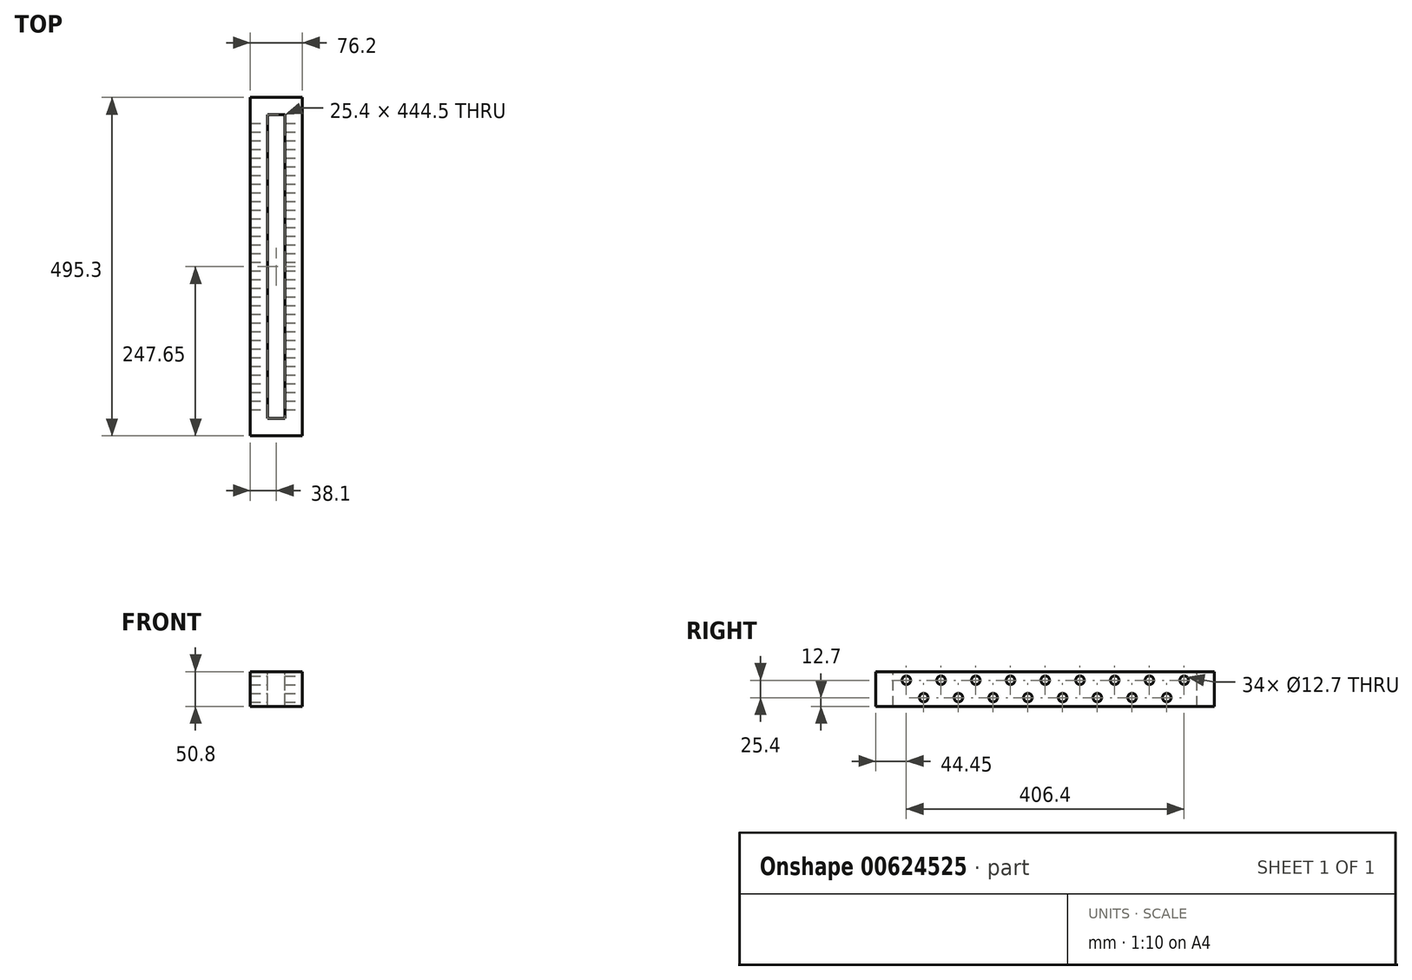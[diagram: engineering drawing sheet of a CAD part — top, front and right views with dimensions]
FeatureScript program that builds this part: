
annotation { "Feature Type Name" : "Feature", "Feature Type Description" : "" }
export const myFeature = defineFeature(function(context is Context, id is Id, definition is map)
    precondition{}
    {
        {
            var Q0;
            Q0=qCreatedBy(makeId("Front.planeOp"),FACE);
            var sketch = newSketch(context, id + "F0", { "sketchPlane" : qUnion([Q0])});
            skLineSegment(sketch, "E0.bottom", {"start": v(0, 0) * mm, "end": v(76.2, 0) * mm});
            skLineSegment(sketch, "E0.top", {"start": v(0, -50.8) * mm, "end": v(76.2, -50.8) * mm});
            skLineSegment(sketch, "E0.left", {"start": v(0, 0) * mm, "end": v(0, -50.8) * mm});
            skLineSegment(sketch, "E0.right", {"start": v(76.2, 0) * mm, "end": v(76.2, -50.8) * mm});
            skSolve(sketch);
        }
        {
            var Q0;
            Q0=makeQuery(id+"F0.imprint","IMPRINT",FACE,{"disambiguationData":[TD([[makeQuery(id+"F0.imprint","IMPRINT",EDGE,{"derivedFrom":sQuery(id+"F0.wireOp",EDGE,"E0.bottom")}),-1.0]])]});
            extrude(context, id + "F1", {"entities" : qUnion([Q0]), "depth" : 495.3 * mm, "offsetDistance" : 25.4 * mm});
        }
        {
            var Q0;
            Q0=makeQuery(id+"F1.opExtrude","SWEPT_FACE",FACE,{"disambiguationData":[OSD([sQuery(id+"F0.wireOp",EDGE,"E0.bottom")])]});
            var sketch = newSketch(context, id + "F2", { "sketchPlane" : qUnion([Q0])});
            skLineSegment(sketch, "E1.bottom", {"start": v(50.8, -469.9) * mm, "end": v(25.4, -469.9) * mm});
            skLineSegment(sketch, "E1.top", {"start": v(50.8, -25.4) * mm, "end": v(25.4, -25.4) * mm});
            skLineSegment(sketch, "E1.left", {"start": v(50.8, -469.9) * mm, "end": v(50.8, -25.4) * mm});
            skLineSegment(sketch, "E1.right", {"start": v(25.4, -469.9) * mm, "end": v(25.4, -25.4) * mm});
            skSolve(sketch);
        }
        {
            var Q0;
            Q0=makeQuery(id+"F2.imprint","IMPRINT",FACE,{"disambiguationData":[TD([[makeQuery(id+"F2.imprint","IMPRINT",EDGE,{"derivedFrom":sQuery(id+"F2.wireOp",EDGE,"E1.bottom")}),-1.0]])]});
            extrude(context, id + "F3", {"entities" : qUnion([Q0]), "operationType" : NewBodyOperationType.REMOVE, "oppositeDirection" : true, "depth" : 50.8 * mm, "offsetDistance" : 25.4 * mm});
        }
        {
            var Q0;
            Q0=makeQuery(id+"F1.opExtrude","SWEPT_FACE",FACE,{"disambiguationData":[OSD([sQuery(id+"F0.wireOp",EDGE,"E0.right")])]});
            var sketch = newSketch(context, id + "F4", { "sketchPlane" : qUnion([Q0])});
            skCircle(sketch, "E2", {"center": v(-450.85, -12.7) * mm, "radius": 6.35 * mm});
            skCircle(sketch, "E3.1.0.0", {"center": v(-400.05, -12.7) * mm, "radius": 6.35 * mm});
            skCircle(sketch, "E3.2.0.0", {"center": v(-349.25, -12.7) * mm, "radius": 6.35 * mm});
            skCircle(sketch, "E3.3.0.0", {"center": v(-298.45, -12.7) * mm, "radius": 6.35 * mm});
            skCircle(sketch, "E3.4.0.0", {"center": v(-247.65, -12.7) * mm, "radius": 6.35 * mm});
            skCircle(sketch, "E3.5.0.0", {"center": v(-196.85, -12.7) * mm, "radius": 6.35 * mm});
            skCircle(sketch, "E3.6.0.0", {"center": v(-146.05, -12.7) * mm, "radius": 6.35 * mm});
            skCircle(sketch, "E3.7.0.0", {"center": v(-95.25, -12.7) * mm, "radius": 6.35 * mm});
            skCircle(sketch, "E3.8.0.0", {"center": v(-44.45, -12.7) * mm, "radius": 6.35 * mm});
            skLineSegment(sketch, "E3.direction1", {"start": v(-450.85, -12.7) * mm, "end": v(-400.05, -12.7) * mm, "construction": true});
            skCircle(sketch, "E4", {"center": v(-425.45, -38.1) * mm, "radius": 6.35 * mm});
            skCircle(sketch, "E5.1.0.0", {"center": v(-374.65, -38.1) * mm, "radius": 6.35 * mm});
            skCircle(sketch, "E5.2.0.0", {"center": v(-323.85, -38.1) * mm, "radius": 6.35 * mm});
            skCircle(sketch, "E5.3.0.0", {"center": v(-273.05, -38.1) * mm, "radius": 6.35 * mm});
            skCircle(sketch, "E5.4.0.0", {"center": v(-222.25, -38.1) * mm, "radius": 6.35 * mm});
            skCircle(sketch, "E5.5.0.0", {"center": v(-171.45, -38.1) * mm, "radius": 6.35 * mm});
            skCircle(sketch, "E5.6.0.0", {"center": v(-120.65, -38.1) * mm, "radius": 6.35 * mm});
            skCircle(sketch, "E5.7.0.0", {"center": v(-69.85, -38.1) * mm, "radius": 6.35 * mm});
            skLineSegment(sketch, "E5.direction1", {"start": v(-425.45, -38.1) * mm, "end": v(-374.65, -38.1) * mm, "construction": true});
            skSolve(sketch);
        }
        {
            var Q0;
            Q0=makeQuery(id+"F4.imprint","IMPRINT",FACE,{"disambiguationData":[TD([[makeQuery(id+"F4.imprint","IMPRINT",EDGE,{"derivedFrom":sQuery(id+"F4.wireOp",EDGE,"E2")}),1.0]])]});
            var Q1;
            Q1=makeQuery(id+"F4.imprint","IMPRINT",FACE,{"disambiguationData":[TD([[makeQuery(id+"F4.imprint","IMPRINT",EDGE,{"derivedFrom":sQuery(id+"F4.wireOp",EDGE,"E3.1.0.0")}),1.0]])]});
            var Q2;
            Q2=makeQuery(id+"F4.imprint","IMPRINT",FACE,{"disambiguationData":[TD([[makeQuery(id+"F4.imprint","IMPRINT",EDGE,{"derivedFrom":sQuery(id+"F4.wireOp",EDGE,"E3.2.0.0")}),1.0]])]});
            var Q3;
            Q3=makeQuery(id+"F4.imprint","IMPRINT",FACE,{"disambiguationData":[TD([[makeQuery(id+"F4.imprint","IMPRINT",EDGE,{"derivedFrom":sQuery(id+"F4.wireOp",EDGE,"E3.3.0.0")}),1.0]])]});
            var Q4;
            Q4=makeQuery(id+"F4.imprint","IMPRINT",FACE,{"disambiguationData":[TD([[makeQuery(id+"F4.imprint","IMPRINT",EDGE,{"derivedFrom":sQuery(id+"F4.wireOp",EDGE,"E3.4.0.0")}),1.0]])]});
            var Q5;
            Q5=makeQuery(id+"F4.imprint","IMPRINT",FACE,{"disambiguationData":[TD([[makeQuery(id+"F4.imprint","IMPRINT",EDGE,{"derivedFrom":sQuery(id+"F4.wireOp",EDGE,"E3.5.0.0")}),1.0]])]});
            var Q6;
            Q6=makeQuery(id+"F4.imprint","IMPRINT",FACE,{"disambiguationData":[TD([[makeQuery(id+"F4.imprint","IMPRINT",EDGE,{"derivedFrom":sQuery(id+"F4.wireOp",EDGE,"E3.6.0.0")}),1.0]])]});
            var Q7;
            Q7=makeQuery(id+"F4.imprint","IMPRINT",FACE,{"disambiguationData":[TD([[makeQuery(id+"F4.imprint","IMPRINT",EDGE,{"derivedFrom":sQuery(id+"F4.wireOp",EDGE,"E3.7.0.0")}),1.0]])]});
            var Q8;
            Q8=makeQuery(id+"F4.imprint","IMPRINT",FACE,{"disambiguationData":[TD([[makeQuery(id+"F4.imprint","IMPRINT",EDGE,{"derivedFrom":sQuery(id+"F4.wireOp",EDGE,"E3.8.0.0")}),1.0]])]});
            var Q9;
            Q9=makeQuery(id+"F4.imprint","IMPRINT",FACE,{"disambiguationData":[TD([[makeQuery(id+"F4.imprint","IMPRINT",EDGE,{"derivedFrom":sQuery(id+"F4.wireOp",EDGE,"E5.7.0.0")}),1.0]])]});
            var Q10;
            Q10=makeQuery(id+"F4.imprint","IMPRINT",FACE,{"disambiguationData":[TD([[makeQuery(id+"F4.imprint","IMPRINT",EDGE,{"derivedFrom":sQuery(id+"F4.wireOp",EDGE,"E5.6.0.0")}),1.0]])]});
            var Q11;
            Q11=makeQuery(id+"F4.imprint","IMPRINT",FACE,{"disambiguationData":[TD([[makeQuery(id+"F4.imprint","IMPRINT",EDGE,{"derivedFrom":sQuery(id+"F4.wireOp",EDGE,"E5.5.0.0")}),1.0]])]});
            var Q12;
            Q12=makeQuery(id+"F4.imprint","IMPRINT",FACE,{"disambiguationData":[TD([[makeQuery(id+"F4.imprint","IMPRINT",EDGE,{"derivedFrom":sQuery(id+"F4.wireOp",EDGE,"E5.4.0.0")}),1.0]])]});
            var Q13;
            Q13=makeQuery(id+"F4.imprint","IMPRINT",FACE,{"disambiguationData":[TD([[makeQuery(id+"F4.imprint","IMPRINT",EDGE,{"derivedFrom":sQuery(id+"F4.wireOp",EDGE,"E5.3.0.0")}),1.0]])]});
            var Q14;
            Q14=makeQuery(id+"F4.imprint","IMPRINT",FACE,{"disambiguationData":[TD([[makeQuery(id+"F4.imprint","IMPRINT",EDGE,{"derivedFrom":sQuery(id+"F4.wireOp",EDGE,"E5.2.0.0")}),1.0]])]});
            var Q15;
            Q15=makeQuery(id+"F4.imprint","IMPRINT",FACE,{"disambiguationData":[TD([[makeQuery(id+"F4.imprint","IMPRINT",EDGE,{"derivedFrom":sQuery(id+"F4.wireOp",EDGE,"E5.1.0.0")}),1.0]])]});
            var Q16;
            Q16=makeQuery(id+"F4.imprint","IMPRINT",FACE,{"disambiguationData":[TD([[makeQuery(id+"F4.imprint","IMPRINT",EDGE,{"derivedFrom":sQuery(id+"F4.wireOp",EDGE,"E4")}),1.0]])]});
            extrude(context, id + "F5", {"entities" : qUnion([Q0, Q1, Q2, Q3, Q4, Q5, Q6, Q7, Q8, Q9, Q10, Q11, Q12, Q13, Q14, Q15, Q16]), "operationType" : NewBodyOperationType.REMOVE, "oppositeDirection" : true, "depth" : 76.2 * mm, "offsetDistance" : 25.4 * mm});
        }
    });
